# Revit family: COVETYP002
name_source: partatom
category: Furniture
units: mm (PartAtom-declared; Revit-internal decimal feet)

## family parameters
Always vertical = Yes
Cut with Voids When Loaded = No
OmniClass Number = 23.40.20.00
OmniClass Title = General Furniture and Specialties
Render Appearance Source = Family Geometry
Room Calculation Point = No
Shared = No
Work Plane-Based = No

## types (1)
- COVETYP002
    Cost = 36025 $
    Default Elevation = 0 mm  [stored 0 ft]
    Description = 5 x Pierce - Side Chair - Blue Shells - Gray Frame - Glides, 6 x Pierce - Stool 26 - Blue Shells - Gray Frame, 3 x Chatham Cove 58H x 42W x 30D 3-Sided - Right - Powered, 5 x LB LOUNGE 1 SEAT 50"H X 30"W X 30" SOLID BASE, 1 x LB LOUNGE 3 SEAT 50"H X 72"W X 30" SOLID BASE, 2 x Pack fee per Chair is less than multiple of 3, 1 x TBL, RND, 2mm, 30Dx29H, DISC, GLD, 3 x TBL, RND, 2mm, 30Dx42H, DISC, GLD, 1 x TBL, RND, 2mm, 36Dx29H, DISC, GLD, 3 x TBL, SQR, 2mm, 30Dx29H, DISC, GLD
    Exported From CET Designer = Yes
    Manufacturer = AIS
    Model = 3500BU
    Show COVETYP002 = Yes
    VisibilityIndex = 0

note: [stored X ft] marks values corroborated as IEEE doubles in the binary element streams (Revit-internal decimal feet)

## geometry (parser evidence)
native form markers: Sweep x3
no freeform markers — native parametric forms only
